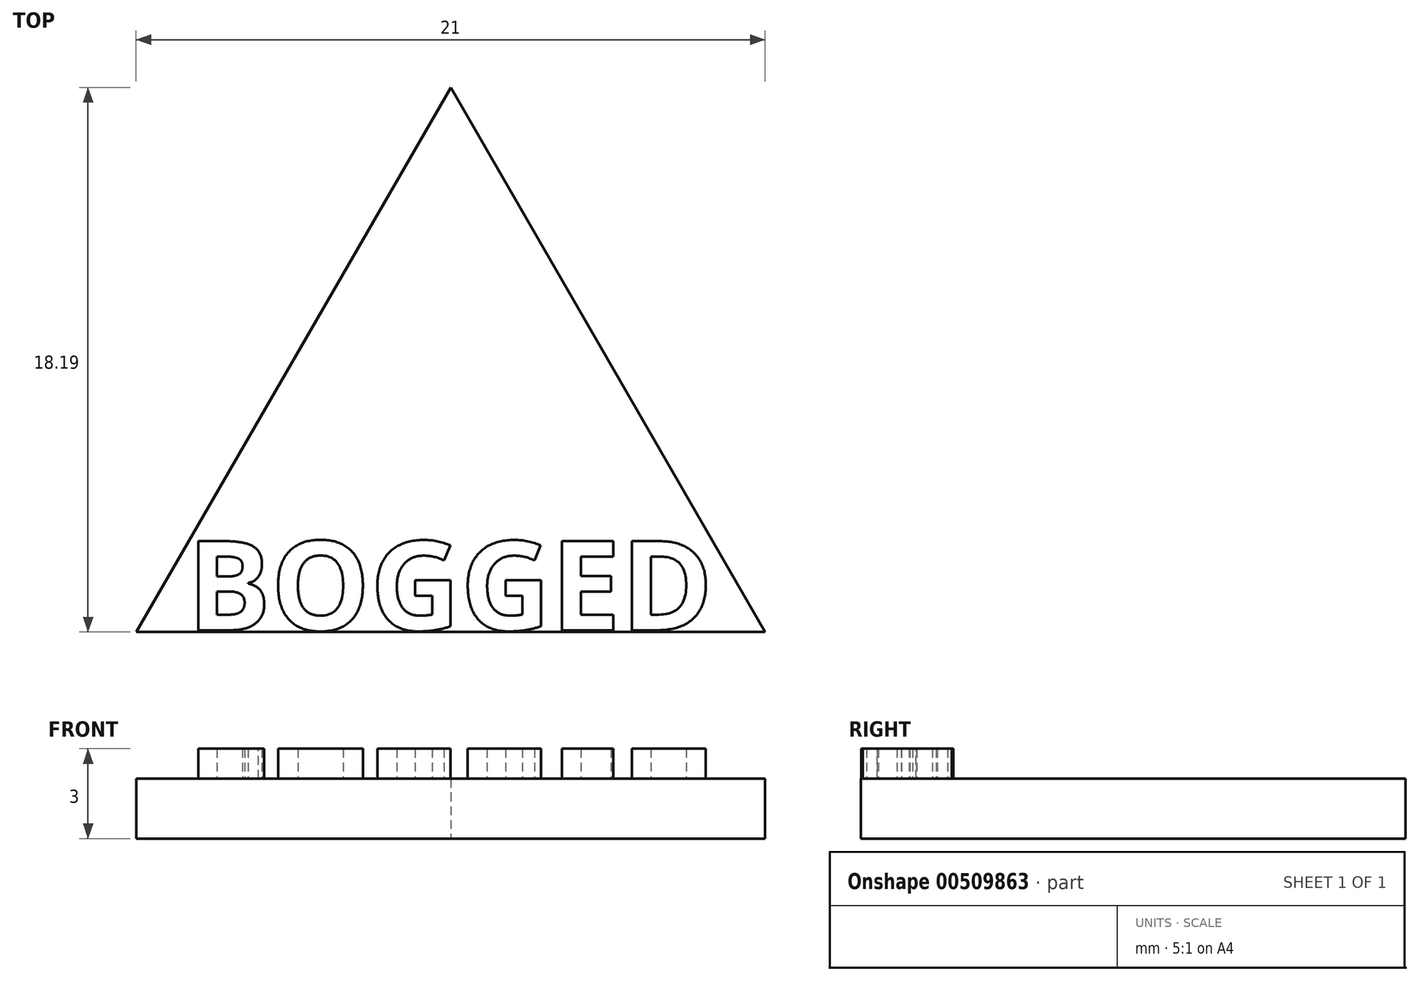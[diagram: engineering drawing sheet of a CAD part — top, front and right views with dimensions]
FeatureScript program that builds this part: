
annotation { "Feature Type Name" : "Feature", "Feature Type Description" : "" }
export const myFeature = defineFeature(function(context is Context, id is Id, definition is map)
    precondition{}
    {
        {
            var Q0;
            Q0=qCreatedBy(makeId("Top.planeOp"),FACE);
            var sketch = newSketch(context, id + "F0", { "sketchPlane" : qUnion([Q0])});
            skLineSegment(sketch, "E0", {"start": v(20.15, -40.42) * mm, "end": v(41.15, -40.42) * mm});
            skLineSegment(sketch, "E1", {"start": v(41.15, -40.42) * mm, "end": v(30.65, -22.23) * mm});
            skLineSegment(sketch, "E2", {"start": v(30.65, -22.23) * mm, "end": v(20.15, -40.42) * mm});
            skSolve(sketch);
        }
        {
            var Q0;
            Q0=qSketchRegion(id+"F0",true);
            extrude(context, id + "F1", {"entities" : qUnion([Q0]), "depth" : 2 * mm, "offsetDistance" : 25 * mm});
        }
        {
            var Q0;
            Q0=makeQuery(id+"F1.opExtrude","CAP_FACE",FACE,{"disambiguationData":[OSD([sQuery(id+"F0.wireOp",EDGE,"E0"),sQuery(id+"F0.wireOp",EDGE,"E1"),sQuery(id+"F0.wireOp",EDGE,"E2")])],"isStart":false});
            var sketch = newSketch(context, id + "F2", { "sketchPlane" : qUnion([Q0])});
            skText(sketch, "E3", { "text": "BOGGED", "fontName": "OpenSans-Bold.ttf"});
            const initialGuessF2  = {"E3": [0.02185, -0.04036, 1, 0, 0.003]};
            skSetInitialGuess(sketch, initialGuessF2);
            skSolve(sketch);
        }
        {
            var Q0;
            Q0 = qSketchRegion(id + "F2", true);
            extrude(context, id + "F3", {"entities" : qUnion([Q0]), "operationType" : NewBodyOperationType.ADD, "depth" : 1 * mm, "offsetDistance" : 25 * mm});
        }
    });
